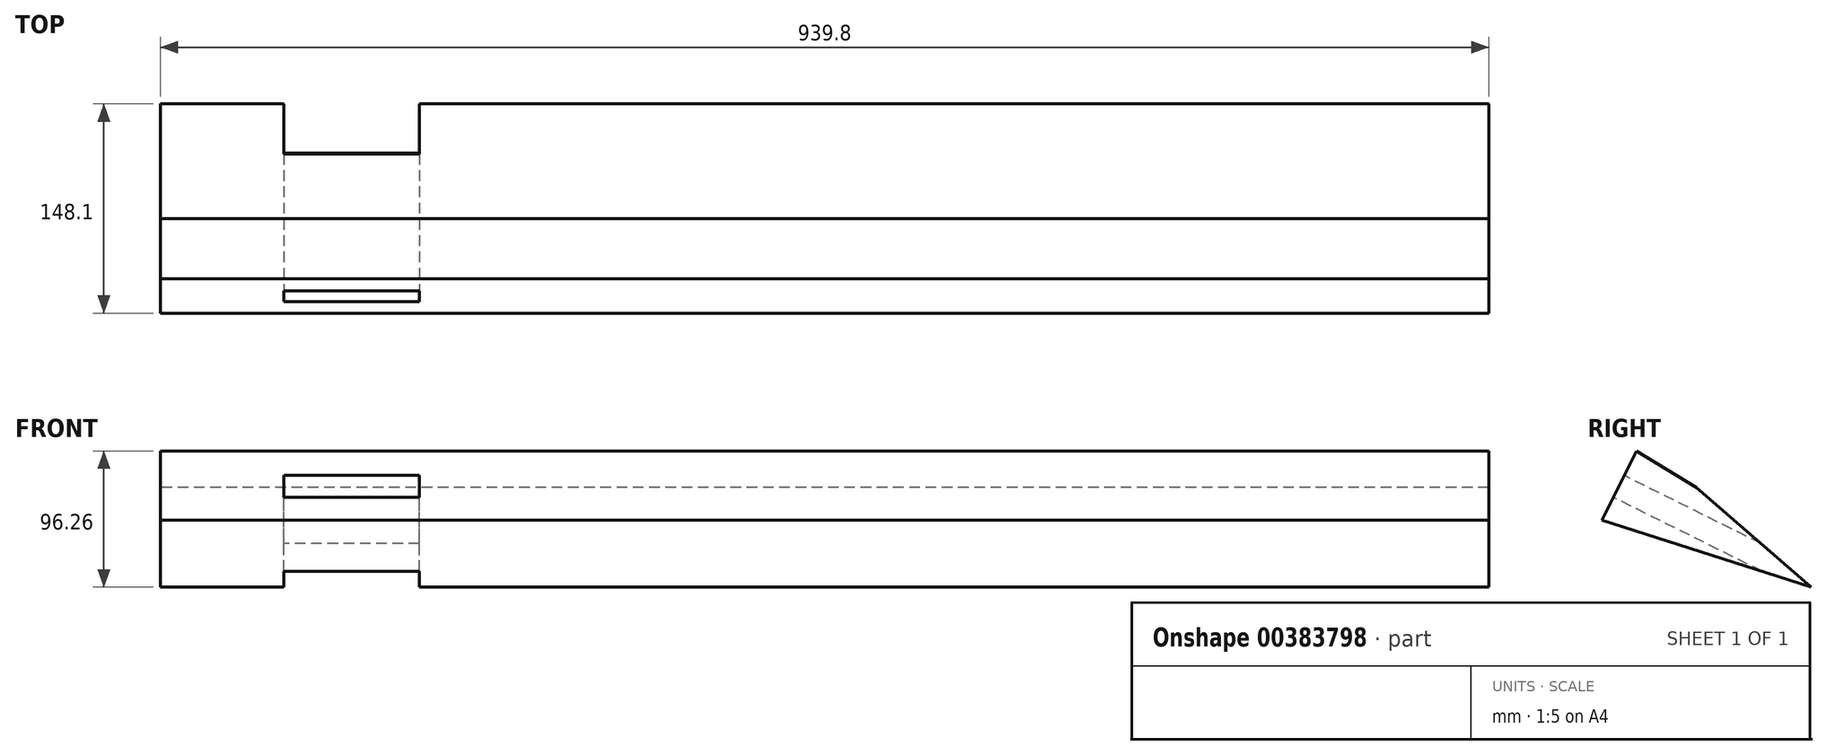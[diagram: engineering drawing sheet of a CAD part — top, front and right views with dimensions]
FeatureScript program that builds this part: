
annotation { "Feature Type Name" : "Feature", "Feature Type Description" : "" }
export const myFeature = defineFeature(function(context is Context, id is Id, definition is map)
    precondition{}
    {
        {
            var Q0;
            Q0=qCreatedBy(makeId("Right.planeOp"),FACE);
            var sketch = newSketch(context, id + "F0", { "sketchPlane" : qUnion([Q0])});
            skLineSegment(sketch, "E0", {"start": v(-40.64, 0) * mm, "end": v(-16.25, 49.05) * mm});
            skLineSegment(sketch, "E1", {"start": v(-16.25, 49.05) * mm, "end": v(26.19, 23.14) * mm});
            skLineSegment(sketch, "E2", {"start": v(26.19, 23.14) * mm, "end": v(107.46, -47.21) * mm});
            skLineSegment(sketch, "E3", {"start": v(107.46, -47.21) * mm, "end": v(-40.64, 0) * mm});
            skSolve(sketch);
        }
        {
            var Q0;
            Q0 = qSketchRegion(id + "F0", true);
            extrude(context, id + "F1", {"entities" : qUnion([Q0]), "depth" : 939.8 * mm});
        }
        {
            var Q0;
            Q0=makeQuery(id+"F1.opExtrude","SWEPT_FACE",FACE,{"disambiguationData":[OSD([sQuery(id+"F0.wireOp",EDGE,"E0")])]});
            var sketch = newSketch(context, id + "F2", { "sketchPlane" : qUnion([Q0])});
            skLineSegment(sketch, "E4.bottom", {"start": v(87.36, 17.28) * mm, "end": v(183.15, 17.28) * mm});
            skLineSegment(sketch, "E4.top", {"start": v(87.36, 0) * mm, "end": v(183.15, 0) * mm});
            skLineSegment(sketch, "E4.left", {"start": v(87.36, 17.28) * mm, "end": v(87.36, 0) * mm});
            skLineSegment(sketch, "E4.right", {"start": v(183.15, 17.28) * mm, "end": v(183.15, 0) * mm});
            skSolve(sketch);
        }
        {
            var Q0;
            Q0 = qSketchRegion(id + "F2", true);
            extrude(context, id + "F3", {"entities" : qUnion([Q0]), "operationType" : NewBodyOperationType.REMOVE, "endBound" : BoundingType.THROUGH_ALL, "oppositeDirection" : true, "depth" : 25.4 * mm});
        }
        {
            var Q0;
            Q0=makeQuery(id+"F1.opExtrude","SWEPT_FACE",FACE,{"disambiguationData":[OSD([sQuery(id+"F0.wireOp",EDGE,"E3")])]});
            var sketch = newSketch(context, id + "F4", { "sketchPlane" : qUnion([Q0])});
            skCircle(sketch, "E5", {"center": v(275.94, -41.05) * mm, "radius": 46.13 * mm});
            skSolve(sketch);
        }
        {
            var Q0;
            Q0 = qSketchRegion(id + "F4", true);
            extrude(context, id + "F5", {"entities" : qUnion([Q0]), "operationType" : NewBodyOperationType.REMOVE, "endBound" : BoundingType.THROUGH_ALL, "depth" : 25.4 * mm});
        }
    });
